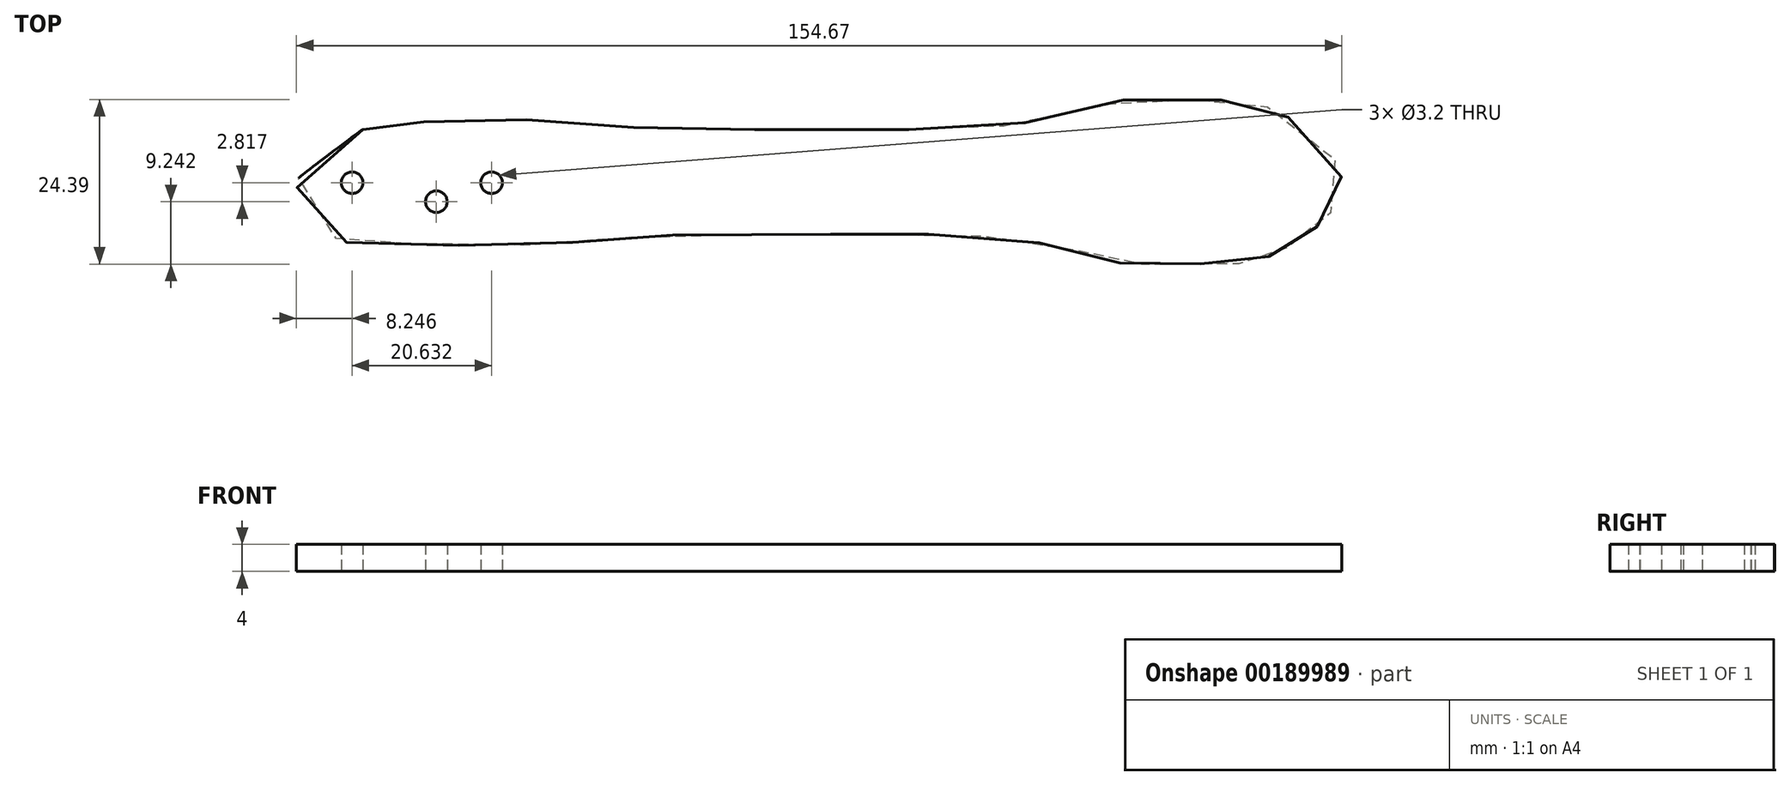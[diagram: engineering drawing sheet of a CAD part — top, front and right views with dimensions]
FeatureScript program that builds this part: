
annotation { "Feature Type Name" : "Feature", "Feature Type Description" : "" }
export const myFeature = defineFeature(function(context is Context, id is Id, definition is map)
    precondition{}
    {
        {
            var Q0;
            Q0=qCreatedBy(makeId("Top.planeOp"),FACE);
            var sketch = newSketch(context, id + "F0", { "sketchPlane" : qUnion([Q0])});
            skLineSegment(sketch, "E0", {"start": v(54.8, -3.9) * mm, "end": v(54.8, 13.58) * mm, "construction": true});
            skLineSegment(sketch, "E1", {"start": v(66.36, -3.84) * mm, "end": v(66.36, 12.93) * mm, "construction": true});
            skLineSegment(sketch, "E2", {"start": v(-48.72, -1.72) * mm, "end": v(-48.72, 12.6) * mm, "construction": true});
            skLineSegment(sketch, "E3", {"start": v(-69.35, -1.5) * mm, "end": v(-69.35, 12.87) * mm, "construction": true});
            skLineSegment(sketch, "E4", {"start": v(-69.35, 0) * mm, "end": v(-48.72, 0) * mm, "construction": true});
            skLineSegment(sketch, "E5", {"start": v(-48.72, 0) * mm, "end": v(-56.51, -2.9) * mm, "construction": true});
            skLineSegment(sketch, "E6", {"start": v(-69.35, 0) * mm, "end": v(-56.88, -2.82) * mm, "construction": true});
            skSolve(sketch);
        }
        {
            var Q0;
            Q0=qCreatedBy(makeId("Top.planeOp"),FACE);
            var sketch = newSketch(context, id + "F1", { "sketchPlane" : qUnion([Q0])});
            skPoint(sketch, "E7", {"position": v(-66.56, 8.68) * mm});
            skPoint(sketch, "E8", {"position": v(-65.15, 8.8) * mm});
            skPoint(sketch, "E9", {"position": v(-60.16, 8.9) * mm});
            skPoint(sketch, "E10", {"position": v(-54.89, 9.2) * mm});
            skPoint(sketch, "E11", {"position": v(-47.44, 9.4) * mm});
            skPoint(sketch, "E12", {"position": v(-38.58, 9.1) * mm});
            skPoint(sketch, "E13", {"position": v(-31.38, 8.43) * mm});
            skPoint(sketch, "E14", {"position": v(-23.01, 7.94) * mm});
            skPoint(sketch, "E15", {"position": v(-12.89, 7.85) * mm});
            skPoint(sketch, "E16", {"position": v(-0.18, 7.85) * mm});
            skPoint(sketch, "E17", {"position": v(16.83, 7.9) * mm});
            skPoint(sketch, "E18", {"position": v(24.53, 8.2) * mm});
            skPoint(sketch, "E19", {"position": v(34.2, 9.5) * mm});
            skPoint(sketch, "E20", {"position": v(42.25, 11.45) * mm});
            skPoint(sketch, "E21", {"position": v(44.84, 12.23) * mm});
            skPoint(sketch, "E22", {"position": v(46.52, 12.33) * mm});
            skPoint(sketch, "E23", {"position": v(54.4, 12.32) * mm});
            skPoint(sketch, "E24", {"position": v(61.48, 12.27) * mm});
            skPoint(sketch, "E25", {"position": v(62.46, 12.27) * mm});
            skPoint(sketch, "E26", {"position": v(65.35, 11.53) * mm});
            skPoint(sketch, "E27", {"position": v(69.92, 9.23) * mm});
            skPoint(sketch, "E28", {"position": v(74.4, 5.78) * mm});
            skPoint(sketch, "E29", {"position": v(76.76, 1.96) * mm});
            skPoint(sketch, "E30", {"position": v(77.07, 0.23) * mm});
            skPoint(sketch, "E31", {"position": v(76.79, -1.82) * mm});
            skPoint(sketch, "E32", {"position": v(75.79, -4) * mm});
            skPoint(sketch, "E33", {"position": v(74.1, -5.85) * mm});
            skPoint(sketch, "E34", {"position": v(72.54, -7.25) * mm});
            skPoint(sketch, "E35", {"position": v(70.5, -8.71) * mm});
            skPoint(sketch, "E36", {"position": v(68.73, -9.75) * mm});
            skPoint(sketch, "E37", {"position": v(66.81, -10.73) * mm});
            skPoint(sketch, "E38", {"position": v(64.96, -11.46) * mm});
            skPoint(sketch, "E39", {"position": v(63.48, -11.9) * mm});
            skPoint(sketch, "E40", {"position": v(61.72, -12.03) * mm});
            skPoint(sketch, "E41", {"position": v(54.35, -12.04) * mm});
            skPoint(sketch, "E42", {"position": v(47.82, -12.05) * mm});
            skPoint(sketch, "E43", {"position": v(45.56, -12.04) * mm});
            skPoint(sketch, "E44", {"position": v(43.9, -11.81) * mm});
            skPoint(sketch, "E45", {"position": v(39.53, -10.52) * mm});
            skPoint(sketch, "E46", {"position": v(34.82, -9.35) * mm});
            skPoint(sketch, "E47", {"position": v(29.16, -8.47) * mm});
            skPoint(sketch, "E48", {"position": v(20.8, -7.77) * mm});
            skPoint(sketch, "E49", {"position": v(10.86, -7.65) * mm});
            skPoint(sketch, "E50", {"position": v(3.89, -7.66) * mm});
            skPoint(sketch, "E51", {"position": v(0.57, -7.64) * mm});
            skPoint(sketch, "E52", {"position": v(-18.65, -7.72) * mm});
            skPoint(sketch, "E53", {"position": v(-27.09, -8.04) * mm});
            skPoint(sketch, "E54", {"position": v(-34.19, -8.64) * mm});
            skPoint(sketch, "E55", {"position": v(-40, -9.07) * mm});
            skPoint(sketch, "E56", {"position": v(-50.02, -9.35) * mm});
            skPoint(sketch, "E57", {"position": v(-58.85, -9.11) * mm});
            skPoint(sketch, "E58", {"position": v(-68.96, -8.92) * mm});
            skPoint(sketch, "E59", {"position": v(-70.76, -8.74) * mm});
            skPoint(sketch, "E60", {"position": v(-71.37, -8.52) * mm});
            skPoint(sketch, "E61", {"position": v(-71.8, -8.17) * mm});
            skPoint(sketch, "E62", {"position": v(-77.08, -1.38) * mm});
            skPoint(sketch, "E63", {"position": v(-77.58, -0.45) * mm});
            skPoint(sketch, "E64", {"position": v(-77.56, 0.25) * mm});
            skPoint(sketch, "E65", {"position": v(-67.4, 8.15) * mm});
            skPoint(sketch, "E66", {"position": v(-67.78, 7.88) * mm});
            skPoint(sketch, "E67", {"position": v(-76.67, 1.2) * mm});
            skFitSpline(sketch, "E68", {"points": [v(-67.78, 7.88) * mm, v(-67.4, 8.15) * mm, v(-66.56, 8.68) * mm, v(-65.15, 8.8) * mm, v(-60.16, 8.9) * mm, v(-54.89, 9.2) * mm, v(-47.44, 9.4) * mm, v(-38.58, 9.1) * mm, v(-31.38, 8.43) * mm, v(-23.01, 7.94) * mm, v(-12.89, 7.85) * mm, v(-0.18, 7.85) * mm, v(16.83, 7.9) * mm, v(24.53, 8.2) * mm, v(34.2, 9.5) * mm, v(42.25, 11.45) * mm, v(44.84, 12.23) * mm, v(46.52, 12.33) * mm, v(54.4, 12.32) * mm, v(61.48, 12.27) * mm, v(62.46, 12.27) * mm, v(65.35, 11.53) * mm, v(69.92, 9.23) * mm, v(74.4, 5.78) * mm, v(76.76, 1.96) * mm, v(77.07, 0.23) * mm, v(76.79, -1.82) * mm, v(75.79, -4) * mm, v(74.1, -5.85) * mm, v(72.54, -7.25) * mm, v(70.5, -8.71) * mm, v(68.73, -9.75) * mm, v(66.81, -10.73) * mm, v(64.96, -11.46) * mm, v(63.48, -11.9) * mm, v(61.72, -12.03) * mm, v(54.35, -12.04) * mm, v(47.82, -12.05) * mm, v(45.56, -12.04) * mm, v(43.9, -11.81) * mm, v(39.53, -10.52) * mm, v(34.82, -9.35) * mm, v(29.16, -8.47) * mm, v(20.8, -7.77) * mm, v(10.86, -7.65) * mm, v(3.89, -7.66) * mm, v(0.57, -7.64) * mm, v(-18.65, -7.72) * mm, v(-27.09, -8.04) * mm, v(-34.19, -8.64) * mm, v(-40, -9.07) * mm, v(-50.02, -9.35) * mm, v(-58.85, -9.11) * mm, v(-68.96, -8.92) * mm, v(-70.76, -8.74) * mm, v(-71.37, -8.52) * mm, v(-71.8, -8.17) * mm, v(-77.08, -1.38) * mm, v(-77.58, -0.45) * mm, v(-77.56, 0.25) * mm, v(-76.67, 1.2) * mm, v(-67.78, 7.88) * mm]});
            skPoint(sketch, "E69.0", {"position": v(-69.35, 0) * mm});
            skPoint(sketch, "E70.0", {"position": v(-48.72, 0) * mm});
            skCircle(sketch, "E71", {"center": v(-69.35, 0) * mm, "radius": 1.6 * mm});
            skCircle(sketch, "E72", {"center": v(-48.72, 0) * mm, "radius": 1.6 * mm});
            skPoint(sketch, "E73.0", {"position": v(-56.88, -2.82) * mm});
            skCircle(sketch, "E74", {"center": v(-56.88, -2.82) * mm, "radius": 1.6 * mm});
            skSolve(sketch);
        }
        {
            var Q0;
            Q0 = qSketchRegion(id + "F1", true);
            extrude(context, id + "F2", {"entities" : qUnion([Q0]), "depth" : 4 * mm});
        }
    });
